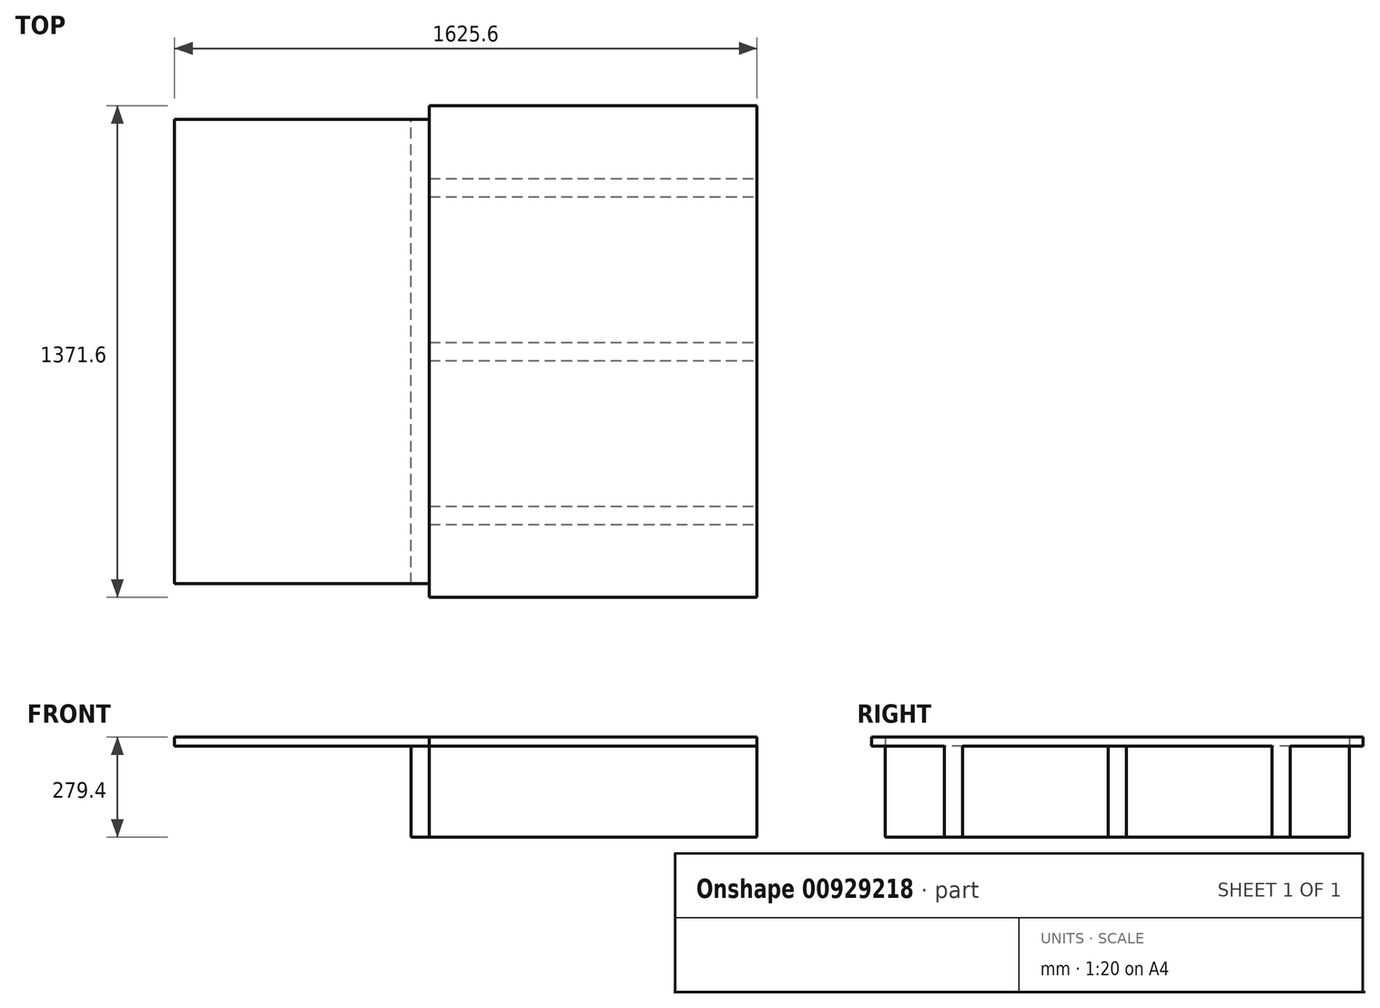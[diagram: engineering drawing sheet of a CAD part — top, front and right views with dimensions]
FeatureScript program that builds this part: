
annotation { "Feature Type Name" : "Feature", "Feature Type Description" : "" }
export const myFeature = defineFeature(function(context is Context, id is Id, definition is map)
    precondition{}
    {
        {
            var Q0;
            Q0=qCreatedBy(makeId("Top.planeOp"),FACE);
            var sketch = newSketch(context, id + "F0", { "sketchPlane" : qUnion([Q0])});
            skLineSegment(sketch, "E0.bottom", {"start": v(457.2, 685.8) * mm, "end": v(-457.2, 685.8) * mm});
            skLineSegment(sketch, "E0.top", {"start": v(457.2, -685.8) * mm, "end": v(-457.2, -685.8) * mm});
            skLineSegment(sketch, "E0.left", {"start": v(457.2, 685.8) * mm, "end": v(457.2, -685.8) * mm});
            skLineSegment(sketch, "E0.right", {"start": v(-457.2, 685.8) * mm, "end": v(-457.2, -685.8) * mm});
            skPoint(sketch, "E0.middle", {"position": v(0, 0) * mm});
            skSolve(sketch);
        }
        {
            var Q0;
            Q0 = qSketchRegion(id + "F0", true);
            extrude(context, id + "F1", {"entities" : qUnion([Q0]), "depth" : 25.4 * mm, "offsetDistance" : 25.4 * mm});
        }
        {
            var Q0;
            Q0=qCreatedBy(makeId("Top.planeOp"),FACE);
            var sketch = newSketch(context, id + "F2", { "sketchPlane" : qUnion([Q0])});
            skLineSegment(sketch, "E1.bottom", {"start": v(-663.38, -618.75) * mm, "end": v(-1323.78, -618.75) * mm});
            skLineSegment(sketch, "E1.top", {"start": v(-663.38, 676.65) * mm, "end": v(-1323.78, 676.65) * mm});
            skLineSegment(sketch, "E1.left", {"start": v(-663.38, -618.75) * mm, "end": v(-663.38, 676.65) * mm});
            skLineSegment(sketch, "E1.right", {"start": v(-1323.78, -618.75) * mm, "end": v(-1323.78, 676.65) * mm});
            skSolve(sketch);
        }
        {
            var Q0;
            Q0 = qSketchRegion(id + "F2", true);
            extrude(context, id + "F3", {"entities" : qUnion([Q0]), "depth" : 25.4 * mm, "offsetDistance" : 25.4 * mm});
        }
        {
            var Q0;
            Q0=qCreatedBy(makeId("Front.planeOp"),FACE);
            var sketch = newSketch(context, id + "F4", { "sketchPlane" : qUnion([Q0])});
            skLineSegment(sketch, "E2.bottom", {"start": v(-457.5, 0) * mm, "end": v(456.9, 0) * mm});
            skLineSegment(sketch, "E2.top", {"start": v(-457.5, -254) * mm, "end": v(456.9, -254) * mm});
            skLineSegment(sketch, "E2.left", {"start": v(-457.5, 0) * mm, "end": v(-457.5, -254) * mm});
            skLineSegment(sketch, "E2.right", {"start": v(456.9, 0) * mm, "end": v(456.9, -254) * mm});
            skSolve(sketch);
        }
        {
            var Q0;
            Q0=makeQuery(id+"F4.imprint","IMPRINT",FACE,{"disambiguationData":[TD([[makeQuery(id+"F4.imprint","IMPRINT",EDGE,{"derivedFrom":sQuery(id+"F4.wireOp",EDGE,"E2.bottom")}),-1.0]])]});
            extrude(context, id + "F5", {"entities" : qUnion([Q0]), "depth" : 50.8 * mm, "offsetDistance" : 25.4 * mm, "symmetric" : true});
        }
        {
            var Q0;
            Q0=makeQuery(id+"F1.opExtrude","CAP_FACE",FACE,{"disambiguationData":[OSD([sQuery(id+"F0.wireOp",EDGE,"E0.bottom"),sQuery(id+"F0.wireOp",EDGE,"E0.top"),sQuery(id+"F0.wireOp",EDGE,"E0.left"),sQuery(id+"F0.wireOp",EDGE,"E0.right")])],"isStart":true});
            var sketch = newSketch(context, id + "F6", { "sketchPlane" : qUnion([Q0])});
            skLineSegment(sketch, "E3.bottom", {"start": v(-457.2, 685.8) * mm, "end": v(457.2, 685.8) * mm});
            skLineSegment(sketch, "E3.top", {"start": v(-457.2, 482.6) * mm, "end": v(457.2, 482.6) * mm});
            skLineSegment(sketch, "E3.left", {"start": v(-457.2, 685.8) * mm, "end": v(-457.2, 482.6) * mm});
            skLineSegment(sketch, "E3.right", {"start": v(457.2, 685.8) * mm, "end": v(457.2, 482.6) * mm});
            skLineSegment(sketch, "E4.bottom", {"start": v(-457.2, -685.8) * mm, "end": v(457.2, -685.8) * mm});
            skLineSegment(sketch, "E4.top", {"start": v(-457.2, -482.6) * mm, "end": v(457.2, -482.6) * mm});
            skLineSegment(sketch, "E4.left", {"start": v(-457.2, -685.8) * mm, "end": v(-457.2, -482.6) * mm});
            skLineSegment(sketch, "E4.right", {"start": v(457.2, -685.8) * mm, "end": v(457.2, -482.6) * mm});
            skLineSegment(sketch, "E5.top", {"start": v(-457.2, 431.8) * mm, "end": v(457.2, 431.8) * mm});
            skLineSegment(sketch, "E5.left", {"start": v(-457.2, 482.6) * mm, "end": v(-457.2, 431.8) * mm});
            skLineSegment(sketch, "E5.right", {"start": v(457.2, 482.6) * mm, "end": v(457.2, 431.8) * mm});
            skLineSegment(sketch, "E6.top", {"start": v(-457.2, -431.8) * mm, "end": v(457.2, -431.8) * mm});
            skLineSegment(sketch, "E6.left", {"start": v(-457.2, -482.6) * mm, "end": v(-457.2, -431.8) * mm});
            skLineSegment(sketch, "E6.right", {"start": v(457.2, -482.6) * mm, "end": v(457.2, -431.8) * mm});
            skSolve(sketch);
        }
        {
            var Q0;
            Q0=makeQuery(id+"F6.imprint","IMPRINT",FACE,{"disambiguationData":[TD([[makeQuery(id+"F6.imprint","IMPRINT",EDGE,{"derivedFrom":sQuery(id+"F6.wireOp",EDGE,"E3.top")}),-1.0]])]});
            var Q1;
            Q1=makeQuery(id+"F6.imprint","IMPRINT",FACE,{"disambiguationData":[TD([[makeQuery(id+"F6.imprint","IMPRINT",EDGE,{"derivedFrom":sQuery(id+"F6.wireOp",EDGE,"E4.top")}),1.0]])]});
            extrude(context, id + "F7", {"entities" : qUnion([Q0, Q1]), "operationType" : NewBodyOperationType.ADD, "depth" : 254 * mm, "offsetDistance" : 25.4 * mm});
        }
        {
            var Q0;
            Q0=makeQuery(id+"F3.opExtrude","SWEPT_BODY",BODY,{"disambiguationData":[OSD([sQuery(id+"F2.wireOp",EDGE,"E1.bottom"),sQuery(id+"F2.wireOp",EDGE,"E1.top"),sQuery(id+"F2.wireOp",EDGE,"E1.left"),sQuery(id+"F2.wireOp",EDGE,"E1.right")])]});
            deleteBodies(context, id + "F8", {"entities" : qUnion([Q0])});
        }
        {
            var Q0;
            Q0=makeQuery(id+"F7.boolean.opBoolean","MERGE",FACE,{"derivedFrom":[makeQuery(id+"F1.opExtrude","SWEPT_FACE",FACE,{"disambiguationData":[OSD([sQuery(id+"F0.wireOp",EDGE,"E0.right")])]}),makeQuery(id+"F7.opExtrude","SWEPT_FACE",FACE,{"disambiguationData":[OSD([sQuery(id+"F6.wireOp",EDGE,"E5.left")])]}),makeQuery(id+"F7.opExtrude","SWEPT_FACE",FACE,{"disambiguationData":[OSD([sQuery(id+"F6.wireOp",EDGE,"E6.left")])]})]});
            var sketch = newSketch(context, id + "F9", { "sketchPlane" : qUnion([Q0])});
            skLineSegment(sketch, "E7.bottom", {"start": v(-685.8, 25.4) * mm, "end": v(-647.7, 25.4) * mm});
            skLineSegment(sketch, "E7.top", {"start": v(-685.8, -174.15) * mm, "end": v(-647.7, -174.15) * mm});
            skLineSegment(sketch, "E7.left", {"start": v(-685.8, 25.4) * mm, "end": v(-685.8, -174.15) * mm});
            skLineSegment(sketch, "E7.right", {"start": v(-647.7, 25.4) * mm, "end": v(-647.7, -174.15) * mm});
            skLineSegment(sketch, "E8.bottom", {"start": v(685.8, 25.4) * mm, "end": v(647.7, 25.4) * mm});
            skLineSegment(sketch, "E8.top", {"start": v(685.8, -268.77) * mm, "end": v(647.7, -268.77) * mm});
            skLineSegment(sketch, "E8.left", {"start": v(685.8, 25.4) * mm, "end": v(685.8, -268.77) * mm});
            skLineSegment(sketch, "E8.right", {"start": v(647.7, 25.4) * mm, "end": v(647.7, -268.77) * mm});
            skLineSegment(sketch, "E9.bottom", {"start": v(647.7, 25.4) * mm, "end": v(-647.7, 25.4) * mm});
            skLineSegment(sketch, "E9.top", {"start": v(647.7, -254) * mm, "end": v(-647.7, -254) * mm});
            skLineSegment(sketch, "E9.left", {"start": v(647.7, 25.4) * mm, "end": v(647.7, -254) * mm});
            skLineSegment(sketch, "E9.right", {"start": v(-647.7, 25.4) * mm, "end": v(-647.7, -254) * mm});
            skSolve(sketch);
        }
        {
            var Q0;
            {var subQ0=sQuery(id+"F6.wireOp",EDGE,"E6.left");var subQ1=sQuery(id+"F6.wireOp",EDGE,"E4.top");var subQ2=makeQuery(id+"F7.opExtrude","SWEPT_EDGE",EDGE,{"disambiguationData":[OSD([sQuery(id+"F6.wireOp",EDGE,"E4.left"),subQ1,subQ0])]});Q0=makeQuery(id+"F9.imprint","IMPRINT",FACE,{"disambiguationData":[TD([[makeQuery(id+"F9.imprint","IMPRINT",EDGE,{"derivedFrom":subQ2}),1.0]])]});}
            var Q1;
            {var subQ1=sQuery(id+"F6.wireOp",EDGE,"E5.left");var subQ2=sQuery(id+"F6.wireOp",EDGE,"E5.top");var subQ3=sQuery(id+"F0.wireOp",EDGE,"E0.right");var subQ4=makeQuery(id+"F7.opExtrude","SWEPT_EDGE",EDGE,{"disambiguationData":[OSD([subQ3,subQ2,subQ1])]});Q1=makeQuery(id+"F9.imprint","IMPRINT",FACE,{"disambiguationData":[TD([[makeQuery(id+"F9.imprint","IMPRINT",EDGE,{"derivedFrom":subQ4}),1.0]])]});}
            var Q2;
            {var subQ1=sQuery(id+"F6.wireOp",EDGE,"E5.left");var subQ2=sQuery(id+"F6.wireOp",EDGE,"E3.top");var subQ3=makeQuery(id+"F7.opExtrude","SWEPT_EDGE",EDGE,{"disambiguationData":[OSD([sQuery(id+"F6.wireOp",EDGE,"E3.left"),subQ2,subQ1])]});Q2=makeQuery(id+"F9.imprint","IMPRINT",FACE,{"disambiguationData":[TD([[makeQuery(id+"F9.imprint","IMPRINT",EDGE,{"derivedFrom":subQ3}),-1.0]])]});}
            var Q3;
            {var subQ8=sQuery(id+"F9.wireOp",EDGE,"E9.bottom");Q3=makeQuery(id+"F9.imprint","IMPRINT",FACE,{"disambiguationData":[TD([[makeQuery(id+"F9.imprint","IMPRINT",EDGE,{"derivedFrom":subQ8}),-1.0]])]});}
            extrude(context, id + "F10", {"entities" : qUnion([Q0, Q1, Q2, Q3]), "depth" : 50.8 * mm, "offsetDistance" : 25.4 * mm});
        }
        {
            var Q0;
            Q0=makeQuery(id+"F10.opExtrude","CAP_FACE",FACE,{"disambiguationData":[OSD([sQuery(id+"F9.wireOp",EDGE,"E9.bottom"),sQuery(id+"F9.wireOp",EDGE,"E9.top"),sQuery(id+"F9.wireOp",EDGE,"E9.left"),sQuery(id+"F9.wireOp",EDGE,"E9.right")])],"isStart":false});
            var sketch = newSketch(context, id + "F11", { "sketchPlane" : qUnion([Q0])});
            skLineSegment(sketch, "E10.bottom", {"start": v(-647.7, 25.4) * mm, "end": v(647.7, 25.4) * mm});
            skLineSegment(sketch, "E10.top", {"start": v(-647.7, 0) * mm, "end": v(647.7, 0) * mm});
            skLineSegment(sketch, "E10.left", {"start": v(-647.7, 25.4) * mm, "end": v(-647.7, 0) * mm});
            skLineSegment(sketch, "E10.right", {"start": v(647.7, 25.4) * mm, "end": v(647.7, 0) * mm});
            skSolve(sketch);
        }
        {
            var Q0;
            Q0 = qSketchRegion(id + "F11", true);
            extrude(context, id + "F12", {"entities" : qUnion([Q0]), "operationType" : NewBodyOperationType.REMOVE, "oppositeDirection" : true, "depth" : 50.8 * mm, "offsetDistance" : 25.4 * mm});
        }
        {
            var Q0;
            Q0=makeQuery(id+"F12.boolean.opBoolean","COPY",FACE,{"derivedFrom":makeQuery(id+"F12.opExtrude","SWEPT_FACE",FACE,{"disambiguationData":[OSD([sQuery(id+"F11.wireOp",EDGE,"E10.top")])]})});
            var sketch = newSketch(context, id + "F13", { "sketchPlane" : qUnion([Q0])});
            skLineSegment(sketch, "E11.bottom", {"start": v(-457.2, 647.7) * mm, "end": v(-1168.4, 647.7) * mm});
            skLineSegment(sketch, "E11.top", {"start": v(-457.2, -647.7) * mm, "end": v(-1168.4, -647.7) * mm});
            skLineSegment(sketch, "E11.left", {"start": v(-457.2, 647.7) * mm, "end": v(-457.2, -647.7) * mm});
            skLineSegment(sketch, "E11.right", {"start": v(-1168.4, 647.7) * mm, "end": v(-1168.4, -647.7) * mm});
            skSolve(sketch);
        }
        {
            var Q0;
            Q0 = qSketchRegion(id + "F13", true);
            extrude(context, id + "F14", {"entities" : qUnion([Q0]), "depth" : 25.4 * mm, "offsetDistance" : 25.4 * mm});
        }
    });
